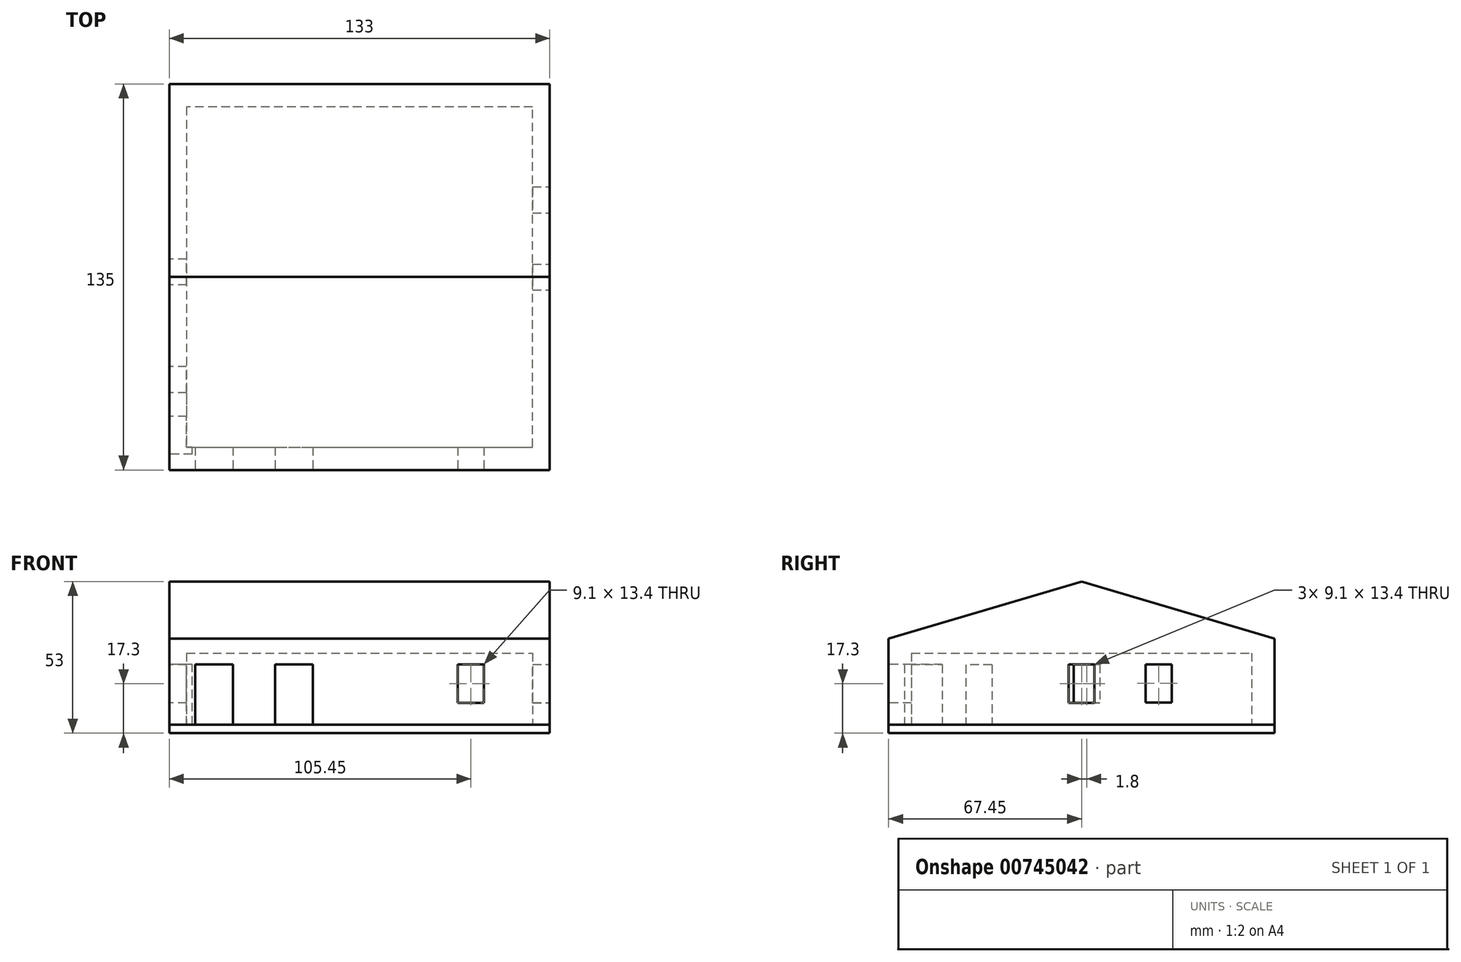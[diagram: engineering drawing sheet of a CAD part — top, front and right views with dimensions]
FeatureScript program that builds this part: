
annotation { "Feature Type Name" : "Feature", "Feature Type Description" : "" }
export const myFeature = defineFeature(function(context is Context, id is Id, definition is map)
    precondition{}
    {
        {
            var Q0;
            Q0=qCreatedBy(makeId("Top.planeOp"),FACE);
            var sketch = newSketch(context, id + "F0", { "sketchPlane" : qUnion([Q0])});
            skLineSegment(sketch, "E0", {"start": v(0, 0) * mm, "end": v(133, 0) * mm});
            skLineSegment(sketch, "E1", {"start": v(133, 0) * mm, "end": v(133, -135) * mm});
            skLineSegment(sketch, "E2", {"start": v(133, -135) * mm, "end": v(0, -135) * mm});
            skLineSegment(sketch, "E3", {"start": v(0, -135) * mm, "end": v(0, 0) * mm});
            skSolve(sketch);
        }
        {
            var Q0;
            Q0 = qSketchRegion(id + "F0", true);
            extrude(context, id + "F1", {"entities" : qUnion([Q0]), "depth" : 3 * mm, "offsetDistance" : 25.4 * mm});
        }
        {
            var Q0;
            Q0=makeQuery(id+"F1.opExtrude","CAP_FACE",FACE,{"disambiguationData":[OSD([sQuery(id+"F0.wireOp",EDGE,"E0"),sQuery(id+"F0.wireOp",EDGE,"E1"),sQuery(id+"F0.wireOp",EDGE,"E2"),sQuery(id+"F0.wireOp",EDGE,"E3")])],"isStart":false});
            var sketch = newSketch(context, id + "F2", { "sketchPlane" : qUnion([Q0])});
            skLineSegment(sketch, "E4", {"start": v(0, 0) * mm, "end": v(133, 0) * mm});
            skLineSegment(sketch, "E5", {"start": v(133, 0) * mm, "end": v(133, -135) * mm});
            skLineSegment(sketch, "E6", {"start": v(133, -135) * mm, "end": v(0, -135) * mm});
            skLineSegment(sketch, "E7", {"start": v(0, -135) * mm, "end": v(0, 0) * mm});
            skLineSegment(sketch, "E8.0", {"start": v(127, -127) * mm, "end": v(127, -8) * mm});
            skLineSegment(sketch, "E9.0", {"start": v(6, -127) * mm, "end": v(127, -127) * mm});
            skLineSegment(sketch, "E10.0", {"start": v(6, -8) * mm, "end": v(6, -127) * mm});
            skLineSegment(sketch, "E11.0", {"start": v(127, -8) * mm, "end": v(6, -8) * mm});
            skSolve(sketch);
        }
        {
            var Q0;
            Q0 = qSketchRegion(id + "F2", true);
            extrude(context, id + "F3", {"entities" : qUnion([Q0]), "depth" : 25 * mm, "offsetDistance" : 25.4 * mm});
        }
        {
            var Q0;
            Q0=makeQuery(id+"F3.opExtrude","SWEPT_FACE",FACE,{"disambiguationData":[OSD([sQuery(id+"F2.wireOp",EDGE,"E6")])]});
            var sketch = newSketch(context, id + "F4", { "sketchPlane" : qUnion([Q0])});
            skSolve(sketch);
        }
        {
            var Q0;
            Q0=makeQuery(id+"F3.opExtrude","SWEPT_FACE",FACE,{"disambiguationData":[OSD([sQuery(id+"F2.wireOp",EDGE,"E7")])]});
            var sketch = newSketch(context, id + "F5", { "sketchPlane" : qUnion([Q0])});
            skLineSegment(sketch, "E12.bottom", {"start": v(61.2, 24) * mm, "end": v(70.3, 24) * mm});
            skLineSegment(sketch, "E12.top", {"start": v(61.2, 10.6) * mm, "end": v(70.3, 10.6) * mm});
            skLineSegment(sketch, "E12.left", {"start": v(61.2, 24) * mm, "end": v(61.2, 10.6) * mm});
            skLineSegment(sketch, "E12.right", {"start": v(70.3, 24) * mm, "end": v(70.3, 10.6) * mm});
            skSolve(sketch);
        }
        {
            var Q0;
            Q0 = qSketchRegion(id + "F5", true);
            extrude(context, id + "F6", {"entities" : qUnion([Q0]), "operationType" : NewBodyOperationType.REMOVE, "oppositeDirection" : true, "depth" : 25 * mm, "offsetDistance" : 25 * mm});
        }
        {
            var Q0;
            Q0=makeQuery(id+"F3.opExtrude","SWEPT_FACE",FACE,{"disambiguationData":[OSD([sQuery(id+"F2.wireOp",EDGE,"E7")])]});
            var sketch = newSketch(context, id + "F7", { "sketchPlane" : qUnion([Q0])});
            skLineSegment(sketch, "E13.bottom", {"start": v(98.85, 23.85) * mm, "end": v(108, 23.85) * mm});
            skLineSegment(sketch, "E13.top", {"start": v(98.85, 3) * mm, "end": v(108, 3) * mm});
            skLineSegment(sketch, "E13.left", {"start": v(98.85, 23.85) * mm, "end": v(98.85, 3) * mm});
            skLineSegment(sketch, "E13.right", {"start": v(108, 23.85) * mm, "end": v(108, 3) * mm});
            skSolve(sketch);
        }
        {
            var Q0;
            Q0 = qSketchRegion(id + "F7", true);
            extrude(context, id + "F8", {"entities" : qUnion([Q0]), "operationType" : NewBodyOperationType.REMOVE, "oppositeDirection" : true, "depth" : 8 * mm, "offsetDistance" : 25 * mm});
        }
        {
            var Q0;
            Q0=makeQuery(id+"F3.opExtrude","SWEPT_FACE",FACE,{"disambiguationData":[OSD([sQuery(id+"F2.wireOp",EDGE,"E7")])]});
            var sketch = newSketch(context, id + "F9", { "sketchPlane" : qUnion([Q0])});
            skLineSegment(sketch, "E14.bottom", {"start": v(116.22, 24) * mm, "end": v(129.42, 24) * mm});
            skLineSegment(sketch, "E14.top", {"start": v(116.22, 3) * mm, "end": v(129.42, 3) * mm});
            skLineSegment(sketch, "E14.left", {"start": v(116.22, 24) * mm, "end": v(116.22, 3) * mm});
            skLineSegment(sketch, "E14.right", {"start": v(129.42, 24) * mm, "end": v(129.42, 3) * mm});
            skSolve(sketch);
        }
        {
            var Q0;
            Q0 = qSketchRegion(id + "F9", true);
            extrude(context, id + "F10", {"entities" : qUnion([Q0]), "operationType" : NewBodyOperationType.REMOVE, "oppositeDirection" : true, "depth" : 8 * mm, "offsetDistance" : 25 * mm});
        }
        {
            var Q0;
            Q0=makeQuery(id+"F3.opExtrude","SWEPT_FACE",FACE,{"disambiguationData":[OSD([sQuery(id+"F2.wireOp",EDGE,"E5")])]});
            var sketch = newSketch(context, id + "F11", { "sketchPlane" : qUnion([Q0])});
            skLineSegment(sketch, "E15.bottom", {"start": v(-72.1, 24) * mm, "end": v(-63, 24) * mm});
            skLineSegment(sketch, "E15.top", {"start": v(-72.1, 10.6) * mm, "end": v(-63, 10.6) * mm});
            skLineSegment(sketch, "E15.left", {"start": v(-72.1, 24) * mm, "end": v(-72.1, 10.6) * mm});
            skLineSegment(sketch, "E15.right", {"start": v(-63, 24) * mm, "end": v(-63, 10.6) * mm});
            skSolve(sketch);
        }
        {
            var Q0;
            Q0 = qSketchRegion(id + "F11", true);
            extrude(context, id + "F12", {"entities" : qUnion([Q0]), "operationType" : NewBodyOperationType.REMOVE, "oppositeDirection" : true, "depth" : 8 * mm, "offsetDistance" : 25 * mm});
        }
        {
            var Q0;
            Q0=makeQuery(id+"F3.opExtrude","SWEPT_FACE",FACE,{"disambiguationData":[OSD([sQuery(id+"F2.wireOp",EDGE,"E5")])]});
            var sketch = newSketch(context, id + "F13", { "sketchPlane" : qUnion([Q0])});
            skLineSegment(sketch, "E16.bottom", {"start": v(-45.1, 24.08) * mm, "end": v(-36, 24.08) * mm});
            skLineSegment(sketch, "E16.top", {"start": v(-45.1, 10.68) * mm, "end": v(-36, 10.68) * mm});
            skLineSegment(sketch, "E16.left", {"start": v(-45.1, 24.08) * mm, "end": v(-45.1, 10.68) * mm});
            skLineSegment(sketch, "E16.right", {"start": v(-36, 24.08) * mm, "end": v(-36, 10.68) * mm});
            skSolve(sketch);
        }
        {
            var Q0;
            {var subQ0=sQuery(id+"F2.wireOp",EDGE,"E6");Q0=makeQuery(id+"F4.imprint","IMPRINT",FACE,{"disambiguationData":[TD([[makeQuery(id+"F4.imprint","IMPRINT",EDGE,{"derivedFrom":makeQuery(id+"F3.opExtrude","CAP_EDGE",EDGE,{"disambiguationData":[OSD([subQ0])],"isStart":true})}),-1.0]])]});}
            var sketch = newSketch(context, id + "F14", { "sketchPlane" : qUnion([Q0])});
            skSolve(sketch);
        }
        {
            var Q0;
            Q0 = qSketchRegion(id + "F13", true);
            extrude(context, id + "F15", {"entities" : qUnion([Q0]), "operationType" : NewBodyOperationType.REMOVE, "oppositeDirection" : true, "depth" : 8 * mm, "offsetDistance" : 25 * mm});
        }
        {
            var Q0;
            {var subQ0=sQuery(id+"F2.wireOp",EDGE,"E6");Q0=makeQuery(id+"F14.imprint","IMPRINT",FACE,{"disambiguationData":[TD([[makeQuery(id+"F14.imprint","IMPRINT",EDGE,{"derivedFrom":makeQuery(id+"F4.imprint","IMPRINT",EDGE,{"derivedFrom":makeQuery(id+"F3.opExtrude","CAP_EDGE",EDGE,{"disambiguationData":[OSD([subQ0])],"isStart":true})})}),-1.0]])]});}
            var sketch = newSketch(context, id + "F16", { "sketchPlane" : qUnion([Q0])});
            skLineSegment(sketch, "E17.bottom", {"start": v(100.9, 24) * mm, "end": v(110, 24) * mm});
            skLineSegment(sketch, "E17.top", {"start": v(100.9, 10.6) * mm, "end": v(110, 10.6) * mm});
            skLineSegment(sketch, "E17.left", {"start": v(100.9, 24) * mm, "end": v(100.9, 10.6) * mm});
            skLineSegment(sketch, "E17.right", {"start": v(110, 24) * mm, "end": v(110, 10.6) * mm});
            skLineSegment(sketch, "E18.bottom", {"start": v(37, 24) * mm, "end": v(50.2, 24) * mm});
            skLineSegment(sketch, "E18.top", {"start": v(37, 3) * mm, "end": v(50.2, 3) * mm});
            skLineSegment(sketch, "E18.left", {"start": v(37, 24) * mm, "end": v(37, 3) * mm});
            skLineSegment(sketch, "E18.right", {"start": v(50.2, 24) * mm, "end": v(50.2, 3) * mm});
            skLineSegment(sketch, "E19.bottom", {"start": v(9, 24) * mm, "end": v(22.2, 24) * mm});
            skLineSegment(sketch, "E19.top", {"start": v(9, 3) * mm, "end": v(22.2, 3) * mm});
            skLineSegment(sketch, "E19.left", {"start": v(9, 24) * mm, "end": v(9, 3) * mm});
            skLineSegment(sketch, "E19.right", {"start": v(22.2, 24) * mm, "end": v(22.2, 3) * mm});
            skSolve(sketch);
        }
        {
            var Q0;
            Q0 = qSketchRegion(id + "F16", true);
            extrude(context, id + "F17", {"entities" : qUnion([Q0]), "operationType" : NewBodyOperationType.REMOVE, "oppositeDirection" : true, "depth" : 8 * mm, "offsetDistance" : 25 * mm});
        }
        {
            var Q0;
            Q0=makeQuery(id+"F3.opExtrude","CAP_FACE",FACE,{"disambiguationData":[OSD([sQuery(id+"F2.wireOp",EDGE,"E4"),sQuery(id+"F2.wireOp",EDGE,"E5"),sQuery(id+"F2.wireOp",EDGE,"E6"),sQuery(id+"F2.wireOp",EDGE,"E7"),sQuery(id+"F2.wireOp",EDGE,"E8.0"),sQuery(id+"F2.wireOp",EDGE,"E9.0"),sQuery(id+"F2.wireOp",EDGE,"E10.0"),sQuery(id+"F2.wireOp",EDGE,"E11.0")])],"isStart":false});
            var sketch = newSketch(context, id + "F18", { "sketchPlane" : qUnion([Q0])});
            skLineSegment(sketch, "E20", {"start": v(0, 0) * mm, "end": v(0, -135) * mm});
            skLineSegment(sketch, "E21", {"start": v(0, -135) * mm, "end": v(133, -135) * mm});
            skLineSegment(sketch, "E22", {"start": v(133, -135) * mm, "end": v(133, 0) * mm});
            skLineSegment(sketch, "E23", {"start": v(133, 0) * mm, "end": v(0, 0) * mm});
            skSolve(sketch);
        }
        {
            var Q0;
            Q0 = qSketchRegion(id + "F18", true);
            extrude(context, id + "F19", {"entities" : qUnion([Q0]), "operationType" : NewBodyOperationType.ADD, "depth" : 25 * mm, "offsetDistance" : 25 * mm});
        }
        {
            var Q0;
            Q0=makeQuery(id+"F19.boolean.opBoolean","MERGE",FACE,{"derivedFrom":[makeQuery(id+"F3.opExtrude","SWEPT_FACE",FACE,{"disambiguationData":[OSD([sQuery(id+"F2.wireOp",EDGE,"E7")])]}),makeQuery(id+"F19.opExtrude","SWEPT_FACE",FACE,{"disambiguationData":[OSD([sQuery(id+"F18.wireOp",EDGE,"E20")])]})]});
            var sketch = newSketch(context, id + "F20", { "sketchPlane" : qUnion([Q0])});
            skLineSegment(sketch, "E24", {"start": v(67.5, 53) * mm, "end": v(135, 33) * mm});
            skLineSegment(sketch, "E25", {"start": v(135, 33) * mm, "end": v(135, 53) * mm});
            skLineSegment(sketch, "E26", {"start": v(135, 53) * mm, "end": v(67.5, 53) * mm});
            skLineSegment(sketch, "E27", {"start": v(67.5, 53) * mm, "end": v(0, 33) * mm});
            skLineSegment(sketch, "E28", {"start": v(0, 33) * mm, "end": v(0, 53) * mm});
            skLineSegment(sketch, "E29", {"start": v(0, 53) * mm, "end": v(67.5, 53) * mm});
            skSolve(sketch);
        }
        {
            var Q0;
            Q0 = qSketchRegion(id + "F20", true);
            extrude(context, id + "F21", {"entities" : qUnion([Q0]), "operationType" : NewBodyOperationType.REMOVE, "endBound" : BoundingType.THROUGH_ALL, "oppositeDirection" : true, "depth" : 25 * mm, "offsetDistance" : 25 * mm});
        }
    });
